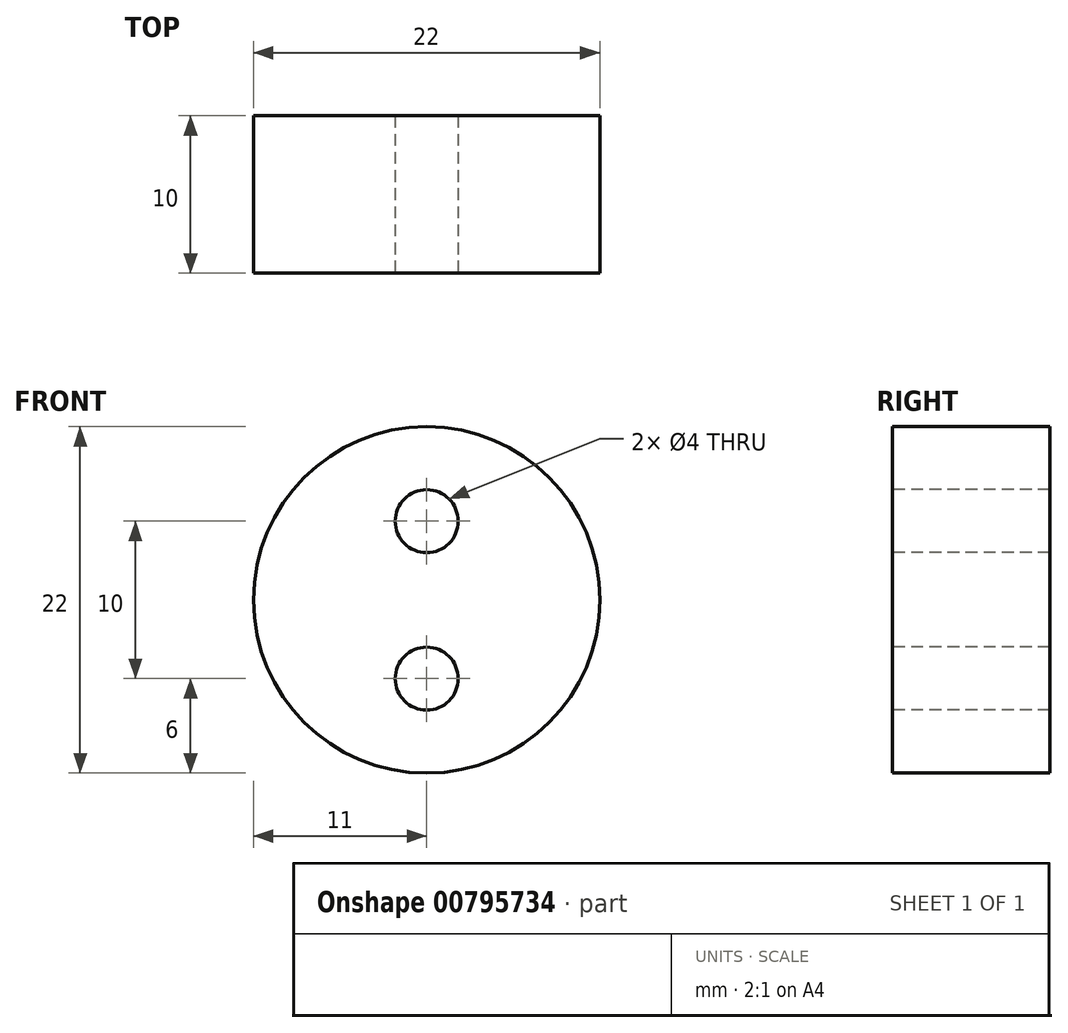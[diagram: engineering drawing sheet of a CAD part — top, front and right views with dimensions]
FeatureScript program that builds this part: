
annotation { "Feature Type Name" : "Feature", "Feature Type Description" : "" }
export const myFeature = defineFeature(function(context is Context, id is Id, definition is map)
    precondition{}
    {
        {
            var Q0;
            Q0=qCreatedBy(makeId("Front.planeOp"),FACE);
            var sketch = newSketch(context, id + "F0", { "sketchPlane" : qUnion([Q0])});
            skCircle(sketch, "E0", {"center": v(0, 0) * mm, "radius": 11 * mm});
            skSolve(sketch);
        }
        {
            var Q0;
            Q0 = qSketchRegion(id + "F0", true);
            extrude(context, id + "F1", {"entities" : qUnion([Q0]), "depth" : 10 * mm, "offsetDistance" : 25 * mm});
        }
        {
            var Q0;
            Q0=makeQuery(id+"F1.opExtrude","CAP_FACE",FACE,{"disambiguationData":[OSD([sQuery(id+"F0.wireOp",EDGE,"E0")])],"isStart":false});
            var sketch = newSketch(context, id + "F2", { "sketchPlane" : qUnion([Q0])});
            skCircle(sketch, "E1", {"center": v(0, 5) * mm, "radius": 2 * mm});
            skCircle(sketch, "E2", {"center": v(0, -5) * mm, "radius": 2 * mm});
            skSolve(sketch);
        }
        {
            var Q0;
            Q0=makeQuery(id+"F2.imprint","IMPRINT",FACE,{"disambiguationData":[TD([[makeQuery(id+"F2.imprint","IMPRINT",EDGE,{"derivedFrom":sQuery(id+"F2.wireOp",EDGE,"E1")}),1.0]])]});
            var Q1;
            Q1=makeQuery(id+"F2.imprint","IMPRINT",FACE,{"disambiguationData":[TD([[makeQuery(id+"F2.imprint","IMPRINT",EDGE,{"derivedFrom":sQuery(id+"F2.wireOp",EDGE,"E2")}),1.0]])]});
            extrude(context, id + "F3", {"entities" : qUnion([Q0, Q1]), "operationType" : NewBodyOperationType.REMOVE, "endBound" : BoundingType.THROUGH_ALL, "oppositeDirection" : true, "depth" : 25 * mm, "offsetDistance" : 25 * mm});
        }
    });
